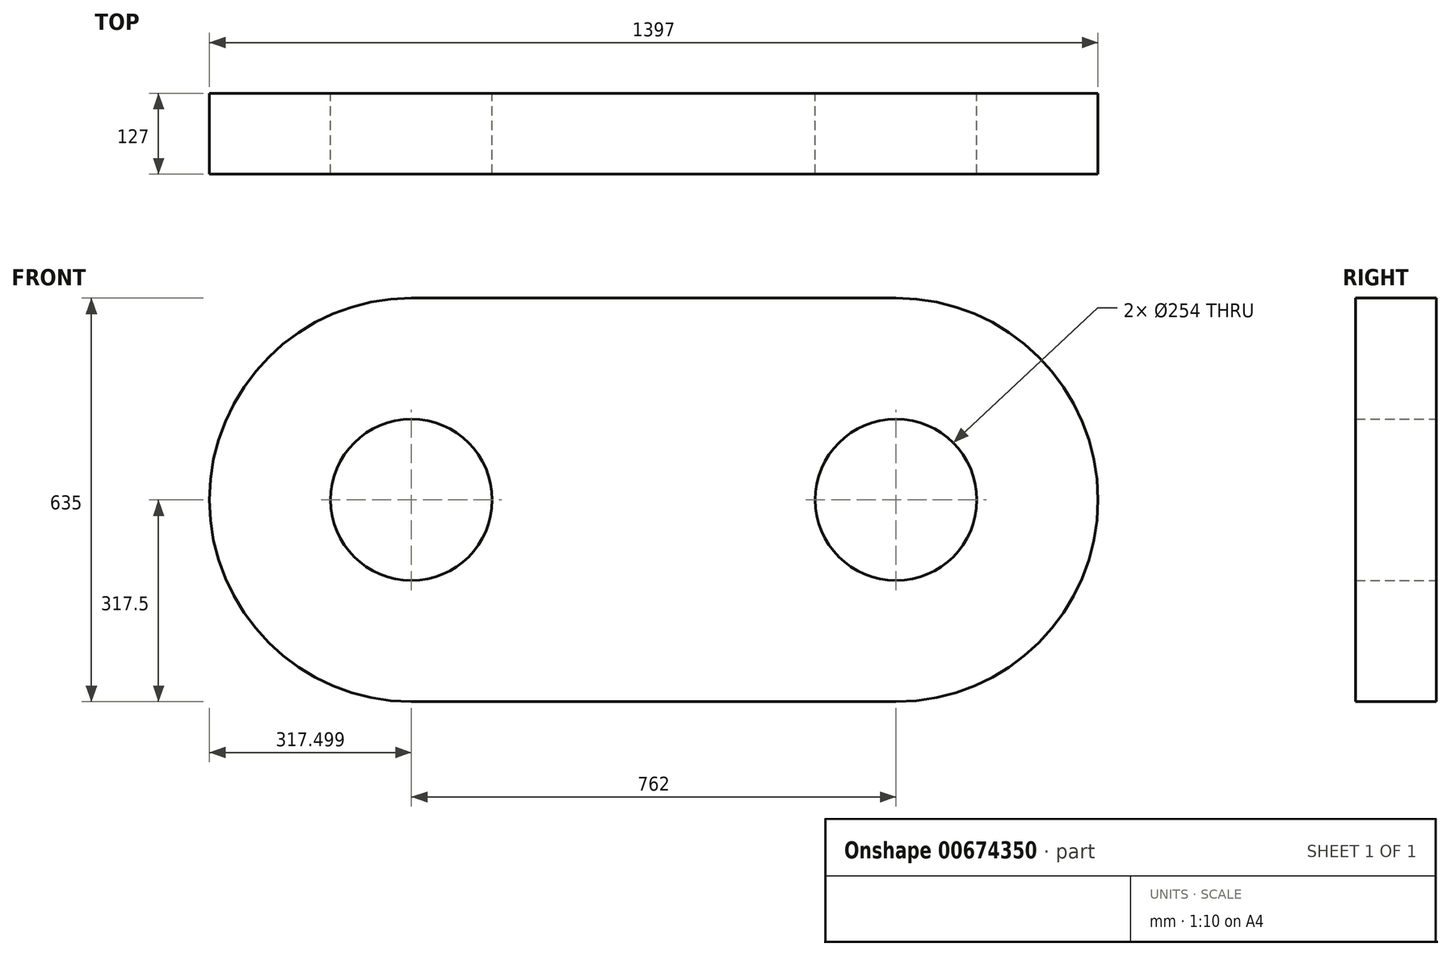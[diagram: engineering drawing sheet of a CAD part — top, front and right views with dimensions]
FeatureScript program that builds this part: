
annotation { "Feature Type Name" : "Feature", "Feature Type Description" : "" }
export const myFeature = defineFeature(function(context is Context, id is Id, definition is map)
    precondition{}
    {
        {
            var Q0;
            Q0=qCreatedBy(makeId("Front.planeOp"),FACE);
            var sketch = newSketch(context, id + "F0", { "sketchPlane" : qUnion([Q0])});
            skLineSegment(sketch, "E0.bottom", {"start": v(397.33, -317.5) * mm, "end": v(-364.67, -317.5) * mm});
            skLineSegment(sketch, "E0.top", {"start": v(397.33, 317.5) * mm, "end": v(-364.67, 317.5) * mm});
            skPoint(sketch, "E0.middle", {"position": v(16.33, 0) * mm});
            skArc(sketch, "E1", {"start": v(-364.67, 317.5) * mm, "mid": v(-682.17, 0) * mm, "end": v(-364.67, -317.5) * mm});
            skArc(sketch, "E2", {"start": v(397.33, -317.5) * mm, "mid": v(714.83, 0) * mm, "end": v(397.33, 317.5) * mm});
            skCircle(sketch, "E3", {"center": v(-364.67, 0) * mm, "radius": 127 * mm});
            skCircle(sketch, "E4", {"center": v(397.33, 0) * mm, "radius": 127 * mm});
            skSolve(sketch);
        }
        {
            var Q0;
            Q0 = qSketchRegion(id + "F0", true);
            extrude(context, id + "F1", {"entities" : qUnion([Q0]), "endBound" : BoundingType.SYMMETRIC, "depth" : 127 * mm, "offsetDistance" : 25.4 * mm});
        }
    });
